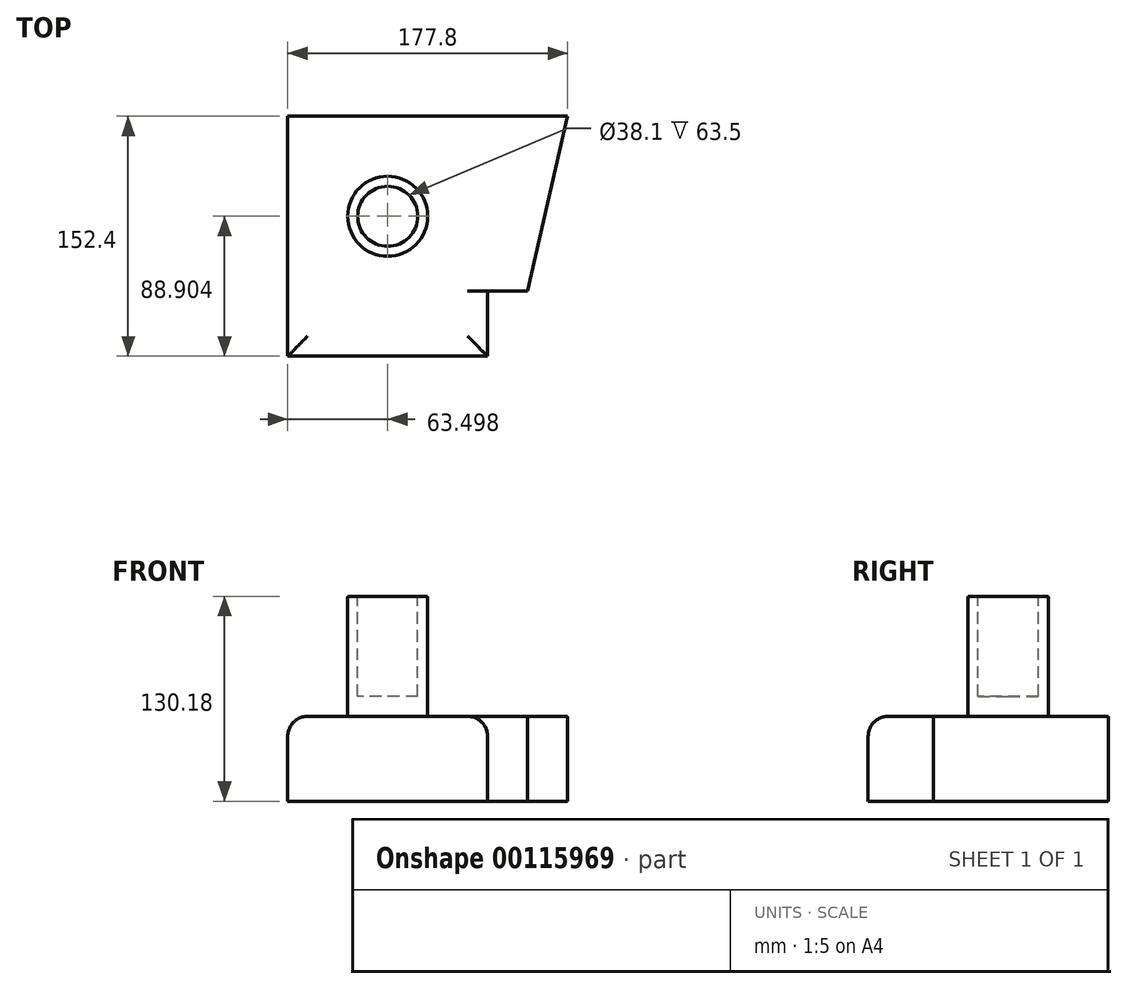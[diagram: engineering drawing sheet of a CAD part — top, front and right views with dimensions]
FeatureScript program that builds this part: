
annotation { "Feature Type Name" : "Feature", "Feature Type Description" : "" }
export const myFeature = defineFeature(function(context is Context, id is Id, definition is map)
    precondition{}
    {
        {
            var Q0;
            Q0=qCreatedBy(makeId("Top.planeOp"),FACE);
            var sketch = newSketch(context, id + "F0", { "sketchPlane" : qUnion([Q0])});
            skLineSegment(sketch, "E0", {"start": v(50.78, -30.15) * mm, "end": v(-76.22, -30.15) * mm});
            skLineSegment(sketch, "E1", {"start": v(-76.22, -30.15) * mm, "end": v(-76.22, 122.25) * mm});
            skLineSegment(sketch, "E2", {"start": v(-76.22, 122.25) * mm, "end": v(101.58, 122.25) * mm});
            skLineSegment(sketch, "E3", {"start": v(50.78, -30.15) * mm, "end": v(50.78, 11.13) * mm});
            skLineSegment(sketch, "E4", {"start": v(50.78, 11.13) * mm, "end": v(76.18, 11.13) * mm});
            skLineSegment(sketch, "E5", {"start": v(76.18, 11.13) * mm, "end": v(101.58, 122.25) * mm});
            skSolve(sketch);
        }
        {
            var Q0;
            Q0=makeQuery(id+"F0.imprint","IMPRINT",FACE,{"disambiguationData":[TD([[makeQuery(id+"F0.imprint","IMPRINT",EDGE,{"derivedFrom":sQuery(id+"F0.wireOp",EDGE,"E0")}),-1.0]])]});
            extrude(context, id + "F1", {"entities" : qUnion([Q0]), "depth" : 53.97 * mm});
        }
        {
            var Q0;
            Q0=makeQuery(id+"F1.opExtrude","CAP_FACE",FACE,{"disambiguationData":[OSD([sQuery(id+"F0.wireOp",EDGE,"E0"),sQuery(id+"F0.wireOp",EDGE,"E1"),sQuery(id+"F0.wireOp",EDGE,"E2"),sQuery(id+"F0.wireOp",EDGE,"E3"),sQuery(id+"F0.wireOp",EDGE,"E4"),sQuery(id+"F0.wireOp",EDGE,"E5")])],"isStart":false});
            var sketch = newSketch(context, id + "F2", { "sketchPlane" : qUnion([Q0])});
            skLineSegment(sketch, "E6", {"start": v(-76.22, 122.25) * mm, "end": v(-76.22, 58.76) * mm});
            skPoint(sketch, "E7", {"position": v(-76.22, 58.76) * mm});
            skLineSegment(sketch, "E8", {"start": v(-76.22, 122.25) * mm, "end": v(-12.71, 122.25) * mm});
            skPoint(sketch, "E9", {"position": v(-12.71, 122.25) * mm});
            skSolve(sketch);
        }
        {
            var Q0;
            {var subQ2=sQuery(id+"F2.wireOp",EDGE,"E6");Q0=makeQuery(id+"F2.imprint","IMPRINT",FACE,{"disambiguationData":[TD([[makeQuery(id+"F2.imprint","IMPRINT",EDGE,{"derivedFrom":subQ2}),-1.0]])]});}
            var sketch = newSketch(context, id + "F3", { "sketchPlane" : qUnion([Q0])});
            skLineSegment(sketch, "E10.top", {"start": v(-76.31, 122.05) * mm, "end": v(-12.72, 122.05) * mm});
            skLineSegment(sketch, "E10.left", {"start": v(-76.31, 58.75) * mm, "end": v(-76.31, 122.05) * mm});
            skCircle(sketch, "E11", {"center": v(-12.72, 58.75) * mm, "radius": 25.4 * mm});
            skSolve(sketch);
        }
        {
            var Q0;
            Q0=makeQuery(id+"F3.imprint","IMPRINT",FACE,{"disambiguationData":[TD([[makeQuery(id+"F3.imprint","IMPRINT",EDGE,{"derivedFrom":sQuery(id+"F3.wireOp",EDGE,"E11")}),1.0]])]});
            extrude(context, id + "F4", {"entities" : qUnion([Q0]), "operationType" : NewBodyOperationType.ADD, "depth" : 76.2 * mm});
        }
        {
            var Q0;
            Q0=makeQuery(id+"F4.opExtrude","CAP_FACE",FACE,{"disambiguationData":[OSD([sQuery(id+"F3.wireOp",EDGE,"E11")])],"isStart":false});
            var sketch = newSketch(context, id + "F5", { "sketchPlane" : qUnion([Q0])});
            skCircle(sketch, "E12", {"center": v(-12.72, 58.75) * mm, "radius": 19.05 * mm});
            skSolve(sketch);
        }
        {
            var Q0;
            Q0 = qSketchRegion(id + "F5", true);
            extrude(context, id + "F6", {"entities" : qUnion([Q0]), "operationType" : NewBodyOperationType.REMOVE, "oppositeDirection" : true, "depth" : 63.5 * mm});
        }
        {
            var Q0;
            Q0=makeQuery(id+"F1.opExtrude","CAP_EDGE",EDGE,{"disambiguationData":[OSD([sQuery(id+"F0.wireOp",EDGE,"E0")])],"isStart":false});
            var Q1;
            Q1=makeQuery(id+"F1.opExtrude","CAP_EDGE",EDGE,{"disambiguationData":[OSD([sQuery(id+"F0.wireOp",EDGE,"E3")])],"isStart":false});
            var Q2;
            Q2=makeQuery(id+"F1.opExtrude","CAP_EDGE",EDGE,{"disambiguationData":[OSD([sQuery(id+"F0.wireOp",EDGE,"E1")])],"isStart":false});
            var Q3;
            Q3=makeQuery(id+"F4.opExtrude","CAP_EDGE",EDGE,{"disambiguationData":[OSD([sQuery(id+"F3.wireOp",EDGE,"E11")])],"isStart":true});
            fillet(context, id + "F7", {"entities" : qUnion([Q0, Q1, Q2, Q3]), "radius" : 12.7 * mm, "tangentPropagation" : true, "allowEdgeOverflow" : false});
        }
    });
